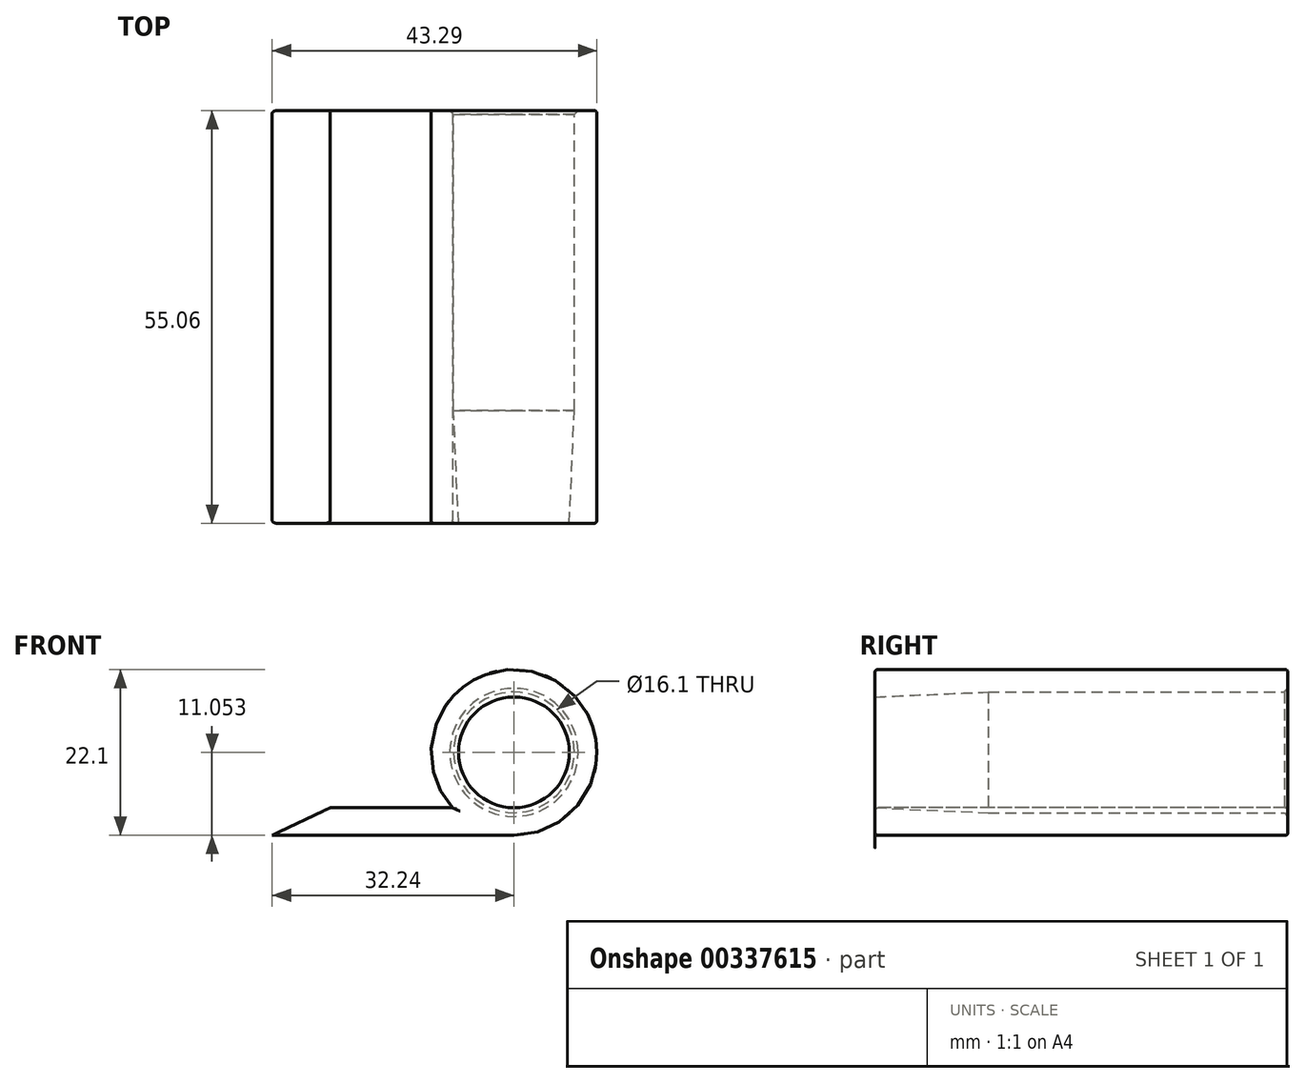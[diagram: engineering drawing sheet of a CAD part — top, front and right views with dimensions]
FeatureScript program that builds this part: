
annotation { "Feature Type Name" : "Feature", "Feature Type Description" : "" }
export const myFeature = defineFeature(function(context is Context, id is Id, definition is map)
    precondition{}
    {
        {
            var Q0;
            Q0=qCreatedBy(makeId("Right.planeOp"),FACE);
            var sketch = newSketch(context, id + "F0", { "sketchPlane" : qUnion([Q0])});
            skLineSegment(sketch, "E0", {"start": v(15.37, 6.68) * mm, "end": v(-24.63, 6.68) * mm});
            skLineSegment(sketch, "E1", {"start": v(-24.63, 6.68) * mm, "end": v(-39.7, 6.03) * mm});
            skLineSegment(sketch, "E2", {"start": v(15.37, 6.68) * mm, "end": v(15.37, 9.68) * mm});
            skLineSegment(sketch, "E3", {"start": v(15.37, 9.68) * mm, "end": v(-39.7, 9.68) * mm});
            skLineSegment(sketch, "E4", {"start": v(-39.7, 9.68) * mm, "end": v(-39.7, 6.03) * mm});
            skLineSegment(sketch, "E5", {"start": v(34.5, -1.37) * mm, "end": v(1.64, -1.37) * mm, "construction": true});
            skSolve(sketch);
        }
        {
            var Q0;
            Q0=makeQuery(id+"F0.imprint","IMPRINT",FACE,{"disambiguationData":[TD([[makeQuery(id+"F0.imprint","IMPRINT",EDGE,{"derivedFrom":sQuery(id+"F0.wireOp",EDGE,"E0")}),-1.0]])]});
            var Q1;
            Q1=sQuery(id+"F0.wireOp",EDGE,"E5");
            revolve(context, id + "F1", {"entities" : qUnion([Q0]), "axis" : qUnion([Q1]), "revolveType" : RevolveType.FULL});
        }
        {
            var Q0;
            Q0=makeQuery(id+"F1.opRevolve","SWEPT_FACE",FACE,{"disambiguationData":[OSD([sQuery(id+"F0.wireOp",EDGE,"E4")])]});
            var sketch = newSketch(context, id + "F2", { "sketchPlane" : qUnion([Q0])});
            skLineSegment(sketch, "E6", {"start": v(0, -12.42) * mm, "end": v(-32.24, -12.42) * mm});
            skLineSegment(sketch, "E7", {"start": v(-32.24, -12.42) * mm, "end": v(-24.52, -8.76) * mm});
            skLineSegment(sketch, "E8", {"start": v(-24.52, -8.76) * mm, "end": v(0, -8.76) * mm});
            skSolve(sketch);
        }
        {
            var Q0;
            {var subQ0=sQuery(id+"F2.wireOp",EDGE,"E6");Q0=makeQuery(id+"F2.imprint","IMPRINT",FACE,{"disambiguationData":[TD([[makeQuery(id+"F2.imprint","IMPRINT",EDGE,{"derivedFrom":subQ0}),-1.0]])]});}
            var Q1;
            Q1=makeQuery(id+"F1.opRevolve","SWEPT_FACE",FACE,{"disambiguationData":[OSD([sQuery(id+"F0.wireOp",EDGE,"E2")])]});
            extrude(context, id + "F3", {"entities" : qUnion([Q0]), "operationType" : NewBodyOperationType.ADD, "endBound" : BoundingType.UP_TO_SURFACE, "oppositeDirection" : true, "endBoundEntityFace" : qUnion([Q1]), "depth" : 25 * mm});
        }
        {
            var Q0;
            Q0=makeQuery(id+"F1.opRevolve","SWEPT_EDGE",EDGE,{"disambiguationData":[OSD([sQuery(id+"F0.wireOp",EDGE,"E3"),sQuery(id+"F0.wireOp",EDGE,"E4")])]});
            var Q1;
            Q1=makeQuery(id+"F3.opExtrude","CAP_EDGE",EDGE,{"disambiguationData":[OSD([sQuery(id+"F2.wireOp",EDGE,"E8")])],"isStart":true});
            var Q2;
            Q2=makeQuery(id+"FlgTL1waQFCH7gW_1.1.F3.opExtrude","CAP_EDGE",EDGE,{"disambiguationData":[OSD([sQuery(id+"F2.wireOp",EDGE,"E8")])],"isStart":true});
            var Q3;
            {var subQ0=sQuery(id+"F2.wireOp",EDGE,"E8");Q3=makeQuery(id+"F3.opExtrude","TWEAK_EDGE",EDGE,{"derivedFrom":[makeQuery(id+"F1.opRevolve","SWEPT_FACE",FACE,{"disambiguationData":[OSD([sQuery(id+"F0.wireOp",EDGE,"E2")])]}),makeQuery(id+"F2.imprint","IMPRINT",EDGE,{"disambiguationData":[TD([[makeQuery(id+"F2.imprint","INTERSECT",VERTEX,{"derivedFrom":[sQuery(id+"F2.wireOp",EDGE,"E7"),subQ0]}),-1.0]])],"derivedFrom":subQ0})]});}
            var Q4;
            Q4=makeQuery(id+"F1.opRevolve","SWEPT_EDGE",EDGE,{"disambiguationData":[OSD([sQuery(id+"F0.wireOp",EDGE,"E2"),sQuery(id+"F0.wireOp",EDGE,"E3")])]});
            var Q5;
            {var subQ0=sQuery(id+"F0.wireOp",EDGE,"E2");var subQ1=sQuery(id+"F2.wireOp",EDGE,"E8");Q5=makeQuery(id+"FlgTL1waQFCH7gW_1.1.F3.opExtrude","TWEAK_EDGE",EDGE,{"derivedFrom":[makeQuery(id+"F2.imprint","IMPRINT",EDGE,{"disambiguationData":[TD([[makeQuery(id+"F2.imprint","INTERSECT",VERTEX,{"derivedFrom":[sQuery(id+"F2.wireOp",EDGE,"E7"),subQ1]}),-1.0]])],"derivedFrom":subQ1}),makeQuery(id+"F3.boolean.opBoolean","MERGE",FACE,{"derivedFrom":[makeQuery(id+"F1.opRevolve","SWEPT_FACE",FACE,{"disambiguationData":[OSD([subQ0])]}),makeQuery(id+"F3.opExtrude","CAP_FACE",FACE,{"disambiguationData":[OSD([subQ0])],"isStart":false})]})]});}
            fillet(context, id + "F4", {"entities" : qUnion([Q0, Q1, Q2, Q3, Q4, Q5]), "radius" : 0.43 * mm, "tangentPropagation" : true, "rho" : 0.5, "crossSection" : FilletCrossSection.CONIC, "allowEdgeOverflow" : false});
        }
        {
            var Q0;
            Q0=makeQuery(id+"F1.opRevolve","SWEPT_EDGE",EDGE,{"disambiguationData":[OSD([sQuery(id+"F0.wireOp",EDGE,"E0"),sQuery(id+"F0.wireOp",EDGE,"E2")])]});
            chamfer(context, id + "F5", {"entities" : qUnion([Q0]), "width" : 0.5 * mm, "tangentPropagation" : true});
        }
    });
